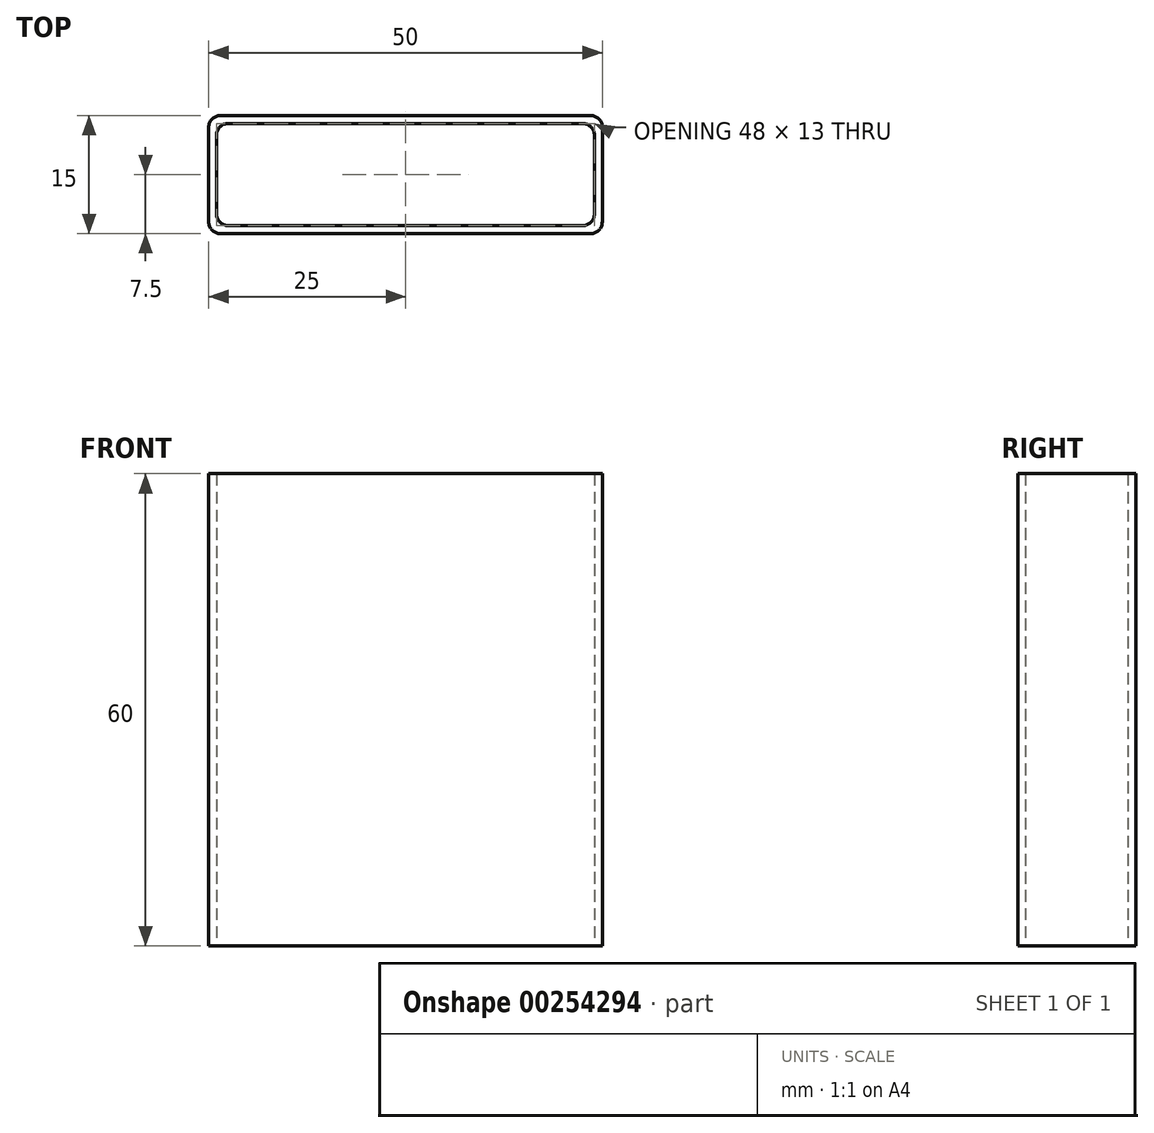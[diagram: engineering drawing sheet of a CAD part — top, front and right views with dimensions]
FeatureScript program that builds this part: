
annotation { "Feature Type Name" : "Feature", "Feature Type Description" : "" }
export const myFeature = defineFeature(function(context is Context, id is Id, definition is map)
    precondition{}
    {
        {
            var Q0;
            Q0=qCreatedBy(makeId("Top.planeOp"),FACE);
            var sketch = newSketch(context, id + "F0", { "sketchPlane" : qUnion([Q0])});
            skLineSegment(sketch, "E0.bottom", {"start": v(25, 7.5) * mm, "end": v(-25, 7.5) * mm});
            skLineSegment(sketch, "E0.top", {"start": v(25, -7.5) * mm, "end": v(-25, -7.5) * mm});
            skLineSegment(sketch, "E0.left", {"start": v(25, 7.5) * mm, "end": v(25, -7.5) * mm});
            skLineSegment(sketch, "E0.right", {"start": v(-25, 7.5) * mm, "end": v(-25, -7.5) * mm});
            skPoint(sketch, "E0.middle", {"position": v(0, 0) * mm});
            skSolve(sketch);
        }
        {
            var Q0;
            Q0=makeQuery(id+"F0.imprint","IMPRINT",FACE,{"disambiguationData":[TD([[makeQuery(id+"F0.imprint","IMPRINT",EDGE,{"derivedFrom":sQuery(id+"F0.wireOp",EDGE,"E0.bottom")}),1.0]])]});
            extrude(context, id + "F1", {"entities" : qUnion([Q0]), "depth" : 60 * mm});
        }
        {
            var Q0;
            Q0=makeQuery(id+"F1.opExtrude","CAP_FACE",FACE,{"disambiguationData":[OSD([sQuery(id+"F0.wireOp",EDGE,"E0.bottom"),sQuery(id+"F0.wireOp",EDGE,"E0.top"),sQuery(id+"F0.wireOp",EDGE,"E0.left"),sQuery(id+"F0.wireOp",EDGE,"E0.right")])],"isStart":false});
            var Q1;
            Q1=makeQuery(id+"F1.opExtrude","CAP_FACE",FACE,{"disambiguationData":[OSD([sQuery(id+"F0.wireOp",EDGE,"E0.bottom"),sQuery(id+"F0.wireOp",EDGE,"E0.top"),sQuery(id+"F0.wireOp",EDGE,"E0.left"),sQuery(id+"F0.wireOp",EDGE,"E0.right")])],"isStart":true});
            shell(context, id + "F2", {"entities" : qUnion([Q0, Q1]), "thickness" : 1 * mm});
        }
        {
            var Q0;
            Q0=makeQuery(id+"F1.opExtrude","SWEPT_EDGE",EDGE,{"disambiguationData":[OSD([sQuery(id+"F0.wireOp",EDGE,"E0.bottom"),sQuery(id+"F0.wireOp",EDGE,"E0.left")])]});
            var Q1;
            Q1=makeQuery(id+"F1.opExtrude","SWEPT_EDGE",EDGE,{"disambiguationData":[OSD([sQuery(id+"F0.wireOp",EDGE,"E0.top"),sQuery(id+"F0.wireOp",EDGE,"E0.left")])]});
            var Q2;
            Q2=makeQuery(id+"F1.opExtrude","SWEPT_EDGE",EDGE,{"disambiguationData":[OSD([sQuery(id+"F0.wireOp",EDGE,"E0.bottom"),sQuery(id+"F0.wireOp",EDGE,"E0.right")])]});
            var Q3;
            Q3=makeQuery(id+"F1.opExtrude","SWEPT_EDGE",EDGE,{"disambiguationData":[OSD([sQuery(id+"F0.wireOp",EDGE,"E0.top"),sQuery(id+"F0.wireOp",EDGE,"E0.right")])]});
            var Q4;
            Q4=makeQuery(id+"F2.opShell","OFFSET_EDGE",EDGE,{"disambiguationData":[OSD([sQuery(id+"F0.wireOp",EDGE,"E0.top"),sQuery(id+"F0.wireOp",EDGE,"E0.right")])]});
            var Q5;
            Q5=makeQuery(id+"F2.opShell","OFFSET_EDGE",EDGE,{"disambiguationData":[OSD([sQuery(id+"F0.wireOp",EDGE,"E0.top"),sQuery(id+"F0.wireOp",EDGE,"E0.left")])]});
            var Q6;
            Q6=makeQuery(id+"F2.opShell","OFFSET_EDGE",EDGE,{"disambiguationData":[OSD([sQuery(id+"F0.wireOp",EDGE,"E0.bottom"),sQuery(id+"F0.wireOp",EDGE,"E0.right")])]});
            var Q7;
            Q7=makeQuery(id+"F2.opShell","OFFSET_EDGE",EDGE,{"disambiguationData":[OSD([sQuery(id+"F0.wireOp",EDGE,"E0.bottom"),sQuery(id+"F0.wireOp",EDGE,"E0.left")])]});
            fillet(context, id + "F3", {"entities" : qUnion([Q0, Q1, Q2, Q3, Q4, Q5, Q6, Q7]), "radius" : 1.5 * mm, "tangentPropagation" : true, "allowEdgeOverflow" : false});
        }
    });
